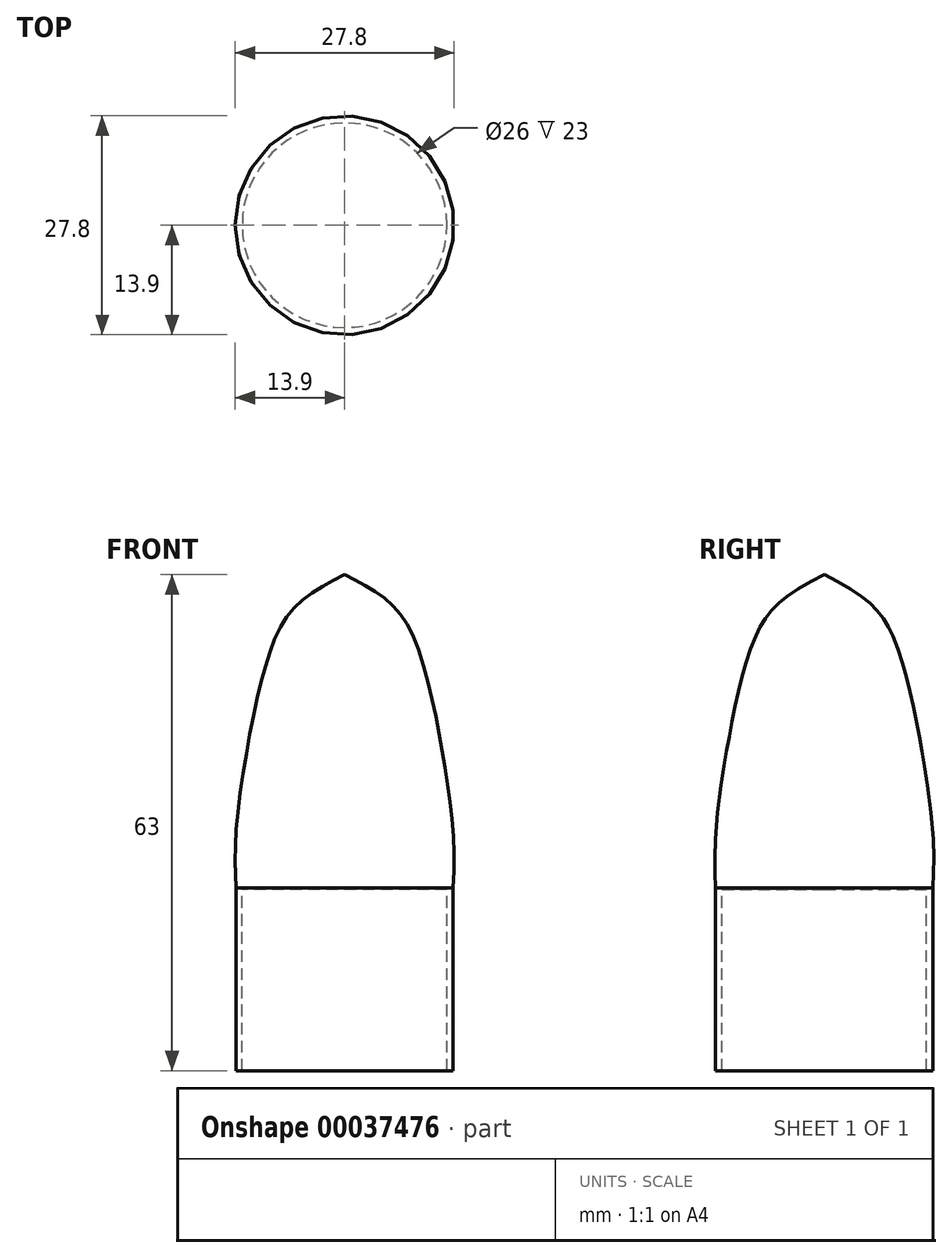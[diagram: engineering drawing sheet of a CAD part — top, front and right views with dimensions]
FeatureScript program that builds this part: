
annotation { "Feature Type Name" : "Feature", "Feature Type Description" : "" }
export const myFeature = defineFeature(function(context is Context, id is Id, definition is map)
    precondition{}
    {
        {
            var Q0;
            Q0=qCreatedBy(makeId("Front.planeOp"),FACE);
            var sketch = newSketch(context, id + "F0", { "sketchPlane" : qUnion([Q0])});
            skLineSegment(sketch, "E0", {"start": v(-13, -0.19) * mm, "end": v(-13, 22.81) * mm});
            skLineSegment(sketch, "E1", {"start": v(-13, -0.19) * mm, "end": v(-13.8, -0.19) * mm});
            skLineSegment(sketch, "E2", {"start": v(-13.8, -0.19) * mm, "end": v(-13.8, 23) * mm});
            skLineSegment(sketch, "E3", {"start": v(-13, 22.81) * mm, "end": v(0, 22.81) * mm});
            skLineSegment(sketch, "E4", {"start": v(0, 22.81) * mm, "end": v(0, 62.81) * mm});
            skFitSpline(sketch, "E5", {"points": [v(-13.8, 23) * mm, v(-13.8, 29.94) * mm, v(-12.16, 41.82) * mm, v(-9.91, 51.7) * mm, v(-7.54, 57.2) * mm, v(-4.41, 60.32) * mm, v(0, 62.81) * mm], "startDerivative": vector(-1.59, 39.26) * mm, "endDerivative": vector(33.11, 16.8) * mm});
            skLineSegment(sketch, "E6", {"start": v(0, 65.2) * mm, "end": v(0, -16.68) * mm});
            skSolve(sketch);
        }
        {
            var Q0;
            Q0=makeQuery(id+"F0.imprint","IMPRINT",FACE,{"disambiguationData":[TD([[makeQuery(id+"F0.imprint","IMPRINT",EDGE,{"derivedFrom":sQuery(id+"F0.wireOp",EDGE,"E0")}),1.0]])]});
            var Q1;
            Q1=sQuery(id+"F0.wireOp",EDGE,"E6");
            revolve(context, id + "F1", {"entities" : qUnion([Q0]), "axis" : qUnion([Q1]), "revolveType" : RevolveType.FULL});
        }
    });
